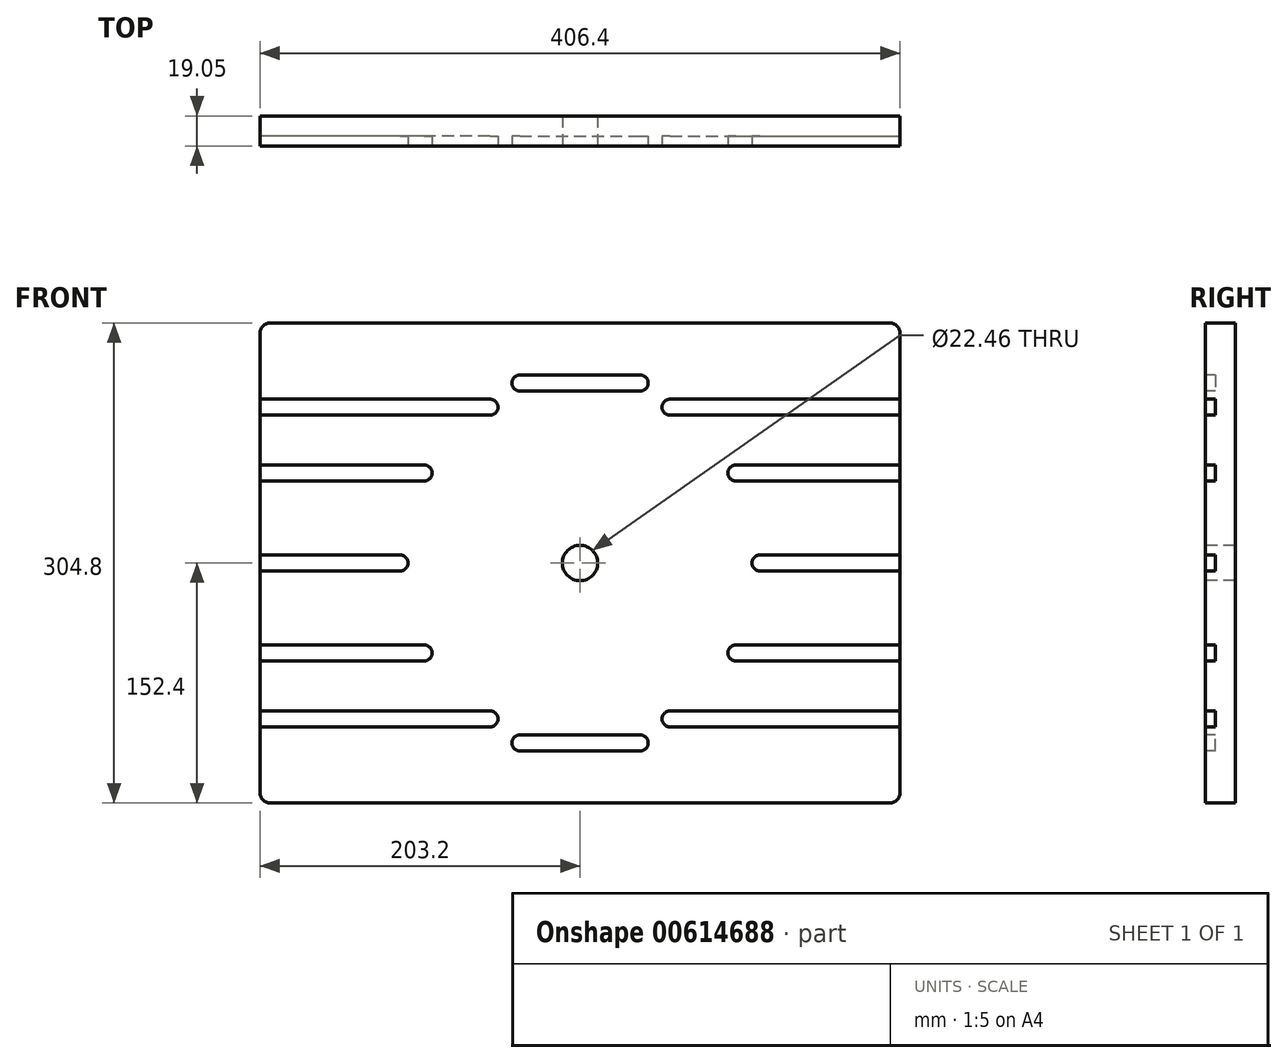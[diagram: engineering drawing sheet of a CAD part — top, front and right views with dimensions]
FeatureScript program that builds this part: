
annotation { "Feature Type Name" : "Feature", "Feature Type Description" : "" }
export const myFeature = defineFeature(function(context is Context, id is Id, definition is map)
    precondition{}
    {
        {
            var Q0;
            Q0=qCreatedBy(makeId("Front.planeOp"),FACE);
            var sketch = newSketch(context, id + "F0", { "sketchPlane" : qUnion([Q0])});
            skLineSegment(sketch, "E0.bottom", {"start": v(203.2, 152.4) * mm, "end": v(-203.2, 152.4) * mm});
            skLineSegment(sketch, "E0.top", {"start": v(203.2, -152.4) * mm, "end": v(-203.2, -152.4) * mm});
            skLineSegment(sketch, "E0.left", {"start": v(203.2, 152.4) * mm, "end": v(203.2, -152.4) * mm});
            skLineSegment(sketch, "E0.right", {"start": v(-203.2, 152.4) * mm, "end": v(-203.2, -152.4) * mm});
            skPoint(sketch, "E0.middle", {"position": v(0, 0) * mm});
            skCircle(sketch, "E1", {"center": v(0, 0) * mm, "radius": 114.3 * mm, "construction": true});
            skLineSegment(sketch, "E2", {"start": v(0, 0) * mm, "end": v(0, 114.3) * mm});
            skLineSegment(sketch, "E3", {"start": v(0, 0) * mm, "end": v(57.15, 98.99) * mm, "construction": true});
            skLineSegment(sketch, "E4", {"start": v(0, 0) * mm, "end": v(98.99, 57.15) * mm, "construction": true});
            skLineSegment(sketch, "E5", {"start": v(0, 0) * mm, "end": v(114.3, 0) * mm, "construction": true});
            skCircle(sketch, "E6", {"center": v(57.15, 98.99) * mm, "radius": 5.08 * mm});
            skLineSegment(sketch, "E7", {"start": v(57.15, 104.07) * mm, "end": v(203.2, 104.07) * mm});
            skLineSegment(sketch, "E8", {"start": v(57.15, 93.9) * mm, "end": v(203.2, 93.9) * mm});
            skCircle(sketch, "E9", {"center": v(98.99, 57.15) * mm, "radius": 5.08 * mm});
            skLineSegment(sketch, "E10", {"start": v(98.99, 62.23) * mm, "end": v(203.2, 62.23) * mm});
            skLineSegment(sketch, "E11", {"start": v(98.99, 52.07) * mm, "end": v(203.2, 52.07) * mm});
            skCircle(sketch, "E12", {"center": v(114.3, 0) * mm, "radius": 5.08 * mm});
            skLineSegment(sketch, "E13", {"start": v(114.3, 5.08) * mm, "end": v(203.2, 5.08) * mm});
            skLineSegment(sketch, "E14", {"start": v(114.3, -5.08) * mm, "end": v(203.2, -5.08) * mm});
            skLineSegment(sketch, "E15", {"start": v(-203.2, 119.38) * mm, "end": v(203.2, 119.38) * mm});
            skLineSegment(sketch, "E16", {"start": v(-203.2, 109.22) * mm, "end": v(203.2, 109.22) * mm});
            skLineSegment(sketch, "E17", {"start": v(0, 0) * mm, "end": v(98.99, -57.15) * mm, "construction": true});
            skLineSegment(sketch, "E18", {"start": v(0, 0) * mm, "end": v(57.15, -98.99) * mm, "construction": true});
            skLineSegment(sketch, "E19", {"start": v(0, 0) * mm, "end": v(0, -114.3) * mm});
            skCircle(sketch, "E20", {"center": v(98.99, -57.15) * mm, "radius": 5.08 * mm});
            skLineSegment(sketch, "E21", {"start": v(98.99, -52.07) * mm, "end": v(203.2, -52.07) * mm});
            skLineSegment(sketch, "E22", {"start": v(98.99, -62.23) * mm, "end": v(203.2, -62.23) * mm});
            skCircle(sketch, "E23", {"center": v(57.15, -98.99) * mm, "radius": 5.08 * mm});
            skLineSegment(sketch, "E24", {"start": v(57.15, -93.9) * mm, "end": v(203.2, -93.9) * mm});
            skLineSegment(sketch, "E25", {"start": v(57.15, -104.07) * mm, "end": v(203.2, -104.07) * mm});
            skArc(sketch, "E26", {"start": v(-38.24, 119.38) * mm, "mid": v(-43.32, 114.3) * mm, "end": v(-38.24, 109.22) * mm});
            skArc(sketch, "E27", {"start": v(-42.56, 116.96) * mm, "mid": v(-42.53, 118.57) * mm, "end": v(-43.92, 119.38) * mm});
            skArc(sketch, "E28", {"start": v(-43.92, 109.22) * mm, "mid": v(-42.53, 110.03) * mm, "end": v(-42.56, 111.64) * mm});
            skArc(sketch, "E29", {"start": v(-12.84, 119.38) * mm, "mid": v(-17.92, 114.3) * mm, "end": v(-12.84, 109.22) * mm});
            skArc(sketch, "E30", {"start": v(12.84, 109.22) * mm, "mid": v(17.92, 114.3) * mm, "end": v(12.84, 119.38) * mm});
            skArc(sketch, "E31", {"start": v(38.24, 109.22) * mm, "mid": v(43.32, 114.3) * mm, "end": v(38.24, 119.38) * mm});
            skLineSegment(sketch, "E32", {"start": v(-12.84, 114.3) * mm, "end": v(12.84, 114.3) * mm});
            skArc(sketch, "E33", {"start": v(43.92, 119.38) * mm, "mid": v(42.53, 118.57) * mm, "end": v(42.56, 116.96) * mm});
            skArc(sketch, "E34", {"start": v(42.56, 111.64) * mm, "mid": v(42.53, 110.03) * mm, "end": v(43.92, 109.22) * mm});
            skCircle(sketch, "E35", {"center": v(0, 0) * mm, "radius": 11.23 * mm});
            skSolve(sketch);
        }
        {
            var Q0;
            Q0 = qSketchRegion(id + "F0", true);
            var Q1;
            {var subQ0=sQuery(id+"F0.wireOp",EDGE,"E6");var subQ1=makeQuery(id+"F0.imprint","INTERSECT",VERTEX,{"derivedFrom":[subQ0,sQuery(id+"F0.wireOp",EDGE,"E7")]});Q1=makeQuery(id+"F0.imprint","IMPRINT",FACE,{"disambiguationData":[TD([[makeQuery(id+"F0.imprint","IMPRINT",EDGE,{"disambiguationData":[TD([[subQ1,-1.0]])],"derivedFrom":subQ0}),1.0]])]});}
            var Q2;
            {var subQ0=sQuery(id+"F0.wireOp",EDGE,"E9");var subQ1=makeQuery(id+"F0.imprint","INTERSECT",VERTEX,{"derivedFrom":[subQ0,sQuery(id+"F0.wireOp",EDGE,"E10")]});Q2=makeQuery(id+"F0.imprint","IMPRINT",FACE,{"disambiguationData":[TD([[makeQuery(id+"F0.imprint","IMPRINT",EDGE,{"disambiguationData":[TD([[subQ1,-1.0]])],"derivedFrom":subQ0}),1.0]])]});}
            var Q3;
            {var subQ0=sQuery(id+"F0.wireOp",EDGE,"E12");var subQ1=makeQuery(id+"F0.imprint","INTERSECT",VERTEX,{"derivedFrom":[subQ0,sQuery(id+"F0.wireOp",EDGE,"E13")]});Q3=makeQuery(id+"F0.imprint","IMPRINT",FACE,{"disambiguationData":[TD([[makeQuery(id+"F0.imprint","IMPRINT",EDGE,{"disambiguationData":[TD([[subQ1,-1.0]])],"derivedFrom":subQ0}),1.0]])]});}
            var Q4;
            {var subQ0=sQuery(id+"F0.wireOp",EDGE,"E20");var subQ1=makeQuery(id+"F0.imprint","INTERSECT",VERTEX,{"derivedFrom":[subQ0,sQuery(id+"F0.wireOp",EDGE,"E21")]});Q4=makeQuery(id+"F0.imprint","IMPRINT",FACE,{"disambiguationData":[TD([[makeQuery(id+"F0.imprint","IMPRINT",EDGE,{"disambiguationData":[TD([[subQ1,-1.0]])],"derivedFrom":subQ0}),1.0]])]});}
            var Q5;
            {var subQ0=sQuery(id+"F0.wireOp",EDGE,"E23");var subQ1=makeQuery(id+"F0.imprint","INTERSECT",VERTEX,{"derivedFrom":[subQ0,sQuery(id+"F0.wireOp",EDGE,"E24")]});Q5=makeQuery(id+"F0.imprint","IMPRINT",FACE,{"disambiguationData":[TD([[makeQuery(id+"F0.imprint","IMPRINT",EDGE,{"disambiguationData":[TD([[subQ1,-1.0]])],"derivedFrom":subQ0}),1.0]])]});}
            var Q6;
            {var subQ3=sQuery(id+"F0.wireOp",EDGE,"E33");Q6=makeQuery(id+"F0.imprint","IMPRINT",FACE,{"disambiguationData":[TD([[makeQuery(id+"F0.imprint","IMPRINT",EDGE,{"derivedFrom":subQ3}),-1.0]])]});}
            var Q7;
            {var subQ4=sQuery(id+"F0.wireOp",EDGE,"E30");Q7=makeQuery(id+"F0.imprint","IMPRINT",FACE,{"disambiguationData":[TD([[makeQuery(id+"F0.imprint","IMPRINT",EDGE,{"derivedFrom":subQ4}),-1.0]])]});}
            var Q8;
            {var subQ3=sQuery(id+"F0.wireOp",EDGE,"E34");Q8=makeQuery(id+"F0.imprint","IMPRINT",FACE,{"disambiguationData":[TD([[makeQuery(id+"F0.imprint","IMPRINT",EDGE,{"derivedFrom":subQ3}),-1.0]])]});}
            var Q9;
            {var subQ3=sQuery(id+"F0.wireOp",EDGE,"E29");Q9=makeQuery(id+"F0.imprint","IMPRINT",FACE,{"disambiguationData":[TD([[makeQuery(id+"F0.imprint","IMPRINT",EDGE,{"derivedFrom":subQ3}),1.0]])]});}
            var Q10;
            {var subQ3=sQuery(id+"F0.wireOp",EDGE,"E27");Q10=makeQuery(id+"F0.imprint","IMPRINT",FACE,{"disambiguationData":[TD([[makeQuery(id+"F0.imprint","IMPRINT",EDGE,{"derivedFrom":subQ3}),-1.0]])]});}
            var Q11;
            {var subQ5=sQuery(id+"F0.wireOp",EDGE,"E29");Q11=makeQuery(id+"F0.imprint","IMPRINT",FACE,{"disambiguationData":[TD([[makeQuery(id+"F0.imprint","IMPRINT",EDGE,{"derivedFrom":subQ5}),-1.0]])]});}
            var Q12;
            {var subQ3=sQuery(id+"F0.wireOp",EDGE,"E28");Q12=makeQuery(id+"F0.imprint","IMPRINT",FACE,{"disambiguationData":[TD([[makeQuery(id+"F0.imprint","IMPRINT",EDGE,{"derivedFrom":subQ3}),-1.0]])]});}
            extrude(context, id + "F1", {"entities" : qUnion([Q0, Q1, Q2, Q3, Q4, Q5, Q6, Q7, Q8, Q9, Q10, Q11, Q12]), "oppositeDirection" : true, "depth" : 19.05 * mm, "offsetDistance" : 25.4 * mm});
        }
        {
            var Q0;
            {var subQ0=sQuery(id+"F0.wireOp",EDGE,"E7");Q0=makeQuery(id+"F0.imprint","IMPRINT",FACE,{"disambiguationData":[TD([[makeQuery(id+"F0.imprint","IMPRINT",EDGE,{"derivedFrom":subQ0}),-1.0]])]});}
            var Q1;
            {var subQ0=sQuery(id+"F0.wireOp",EDGE,"E10");Q1=makeQuery(id+"F0.imprint","IMPRINT",FACE,{"disambiguationData":[TD([[makeQuery(id+"F0.imprint","IMPRINT",EDGE,{"derivedFrom":subQ0}),-1.0]])]});}
            var Q2;
            {var subQ0=sQuery(id+"F0.wireOp",EDGE,"E6");var subQ1=makeQuery(id+"F0.imprint","INTERSECT",VERTEX,{"derivedFrom":[subQ0,sQuery(id+"F0.wireOp",EDGE,"E7")]});Q2=makeQuery(id+"F0.imprint","IMPRINT",FACE,{"disambiguationData":[TD([[makeQuery(id+"F0.imprint","IMPRINT",EDGE,{"disambiguationData":[TD([[subQ1,-1.0]])],"derivedFrom":subQ0}),1.0]])]});}
            var Q3;
            {var subQ0=sQuery(id+"F0.wireOp",EDGE,"E9");var subQ1=makeQuery(id+"F0.imprint","INTERSECT",VERTEX,{"derivedFrom":[subQ0,sQuery(id+"F0.wireOp",EDGE,"E10")]});Q3=makeQuery(id+"F0.imprint","IMPRINT",FACE,{"disambiguationData":[TD([[makeQuery(id+"F0.imprint","IMPRINT",EDGE,{"disambiguationData":[TD([[subQ1,-1.0]])],"derivedFrom":subQ0}),1.0]])]});}
            var Q4;
            {var subQ0=sQuery(id+"F0.wireOp",EDGE,"E12");var subQ1=makeQuery(id+"F0.imprint","INTERSECT",VERTEX,{"derivedFrom":[subQ0,sQuery(id+"F0.wireOp",EDGE,"E13")]});Q4=makeQuery(id+"F0.imprint","IMPRINT",FACE,{"disambiguationData":[TD([[makeQuery(id+"F0.imprint","IMPRINT",EDGE,{"disambiguationData":[TD([[subQ1,-1.0]])],"derivedFrom":subQ0}),1.0]])]});}
            var Q5;
            {var subQ0=sQuery(id+"F0.wireOp",EDGE,"E13");Q5=makeQuery(id+"F0.imprint","IMPRINT",FACE,{"disambiguationData":[TD([[makeQuery(id+"F0.imprint","IMPRINT",EDGE,{"derivedFrom":subQ0}),-1.0]])]});}
            var Q6;
            {var subQ0=sQuery(id+"F0.wireOp",EDGE,"E20");var subQ1=makeQuery(id+"F0.imprint","INTERSECT",VERTEX,{"derivedFrom":[subQ0,sQuery(id+"F0.wireOp",EDGE,"E21")]});Q6=makeQuery(id+"F0.imprint","IMPRINT",FACE,{"disambiguationData":[TD([[makeQuery(id+"F0.imprint","IMPRINT",EDGE,{"disambiguationData":[TD([[subQ1,-1.0]])],"derivedFrom":subQ0}),1.0]])]});}
            var Q7;
            {var subQ0=sQuery(id+"F0.wireOp",EDGE,"E21");Q7=makeQuery(id+"F0.imprint","IMPRINT",FACE,{"disambiguationData":[TD([[makeQuery(id+"F0.imprint","IMPRINT",EDGE,{"derivedFrom":subQ0}),-1.0]])]});}
            var Q8;
            {var subQ0=sQuery(id+"F0.wireOp",EDGE,"E23");var subQ1=makeQuery(id+"F0.imprint","INTERSECT",VERTEX,{"derivedFrom":[subQ0,sQuery(id+"F0.wireOp",EDGE,"E24")]});Q8=makeQuery(id+"F0.imprint","IMPRINT",FACE,{"disambiguationData":[TD([[makeQuery(id+"F0.imprint","IMPRINT",EDGE,{"disambiguationData":[TD([[subQ1,-1.0]])],"derivedFrom":subQ0}),1.0]])]});}
            var Q9;
            {var subQ0=sQuery(id+"F0.wireOp",EDGE,"E24");Q9=makeQuery(id+"F0.imprint","IMPRINT",FACE,{"disambiguationData":[TD([[makeQuery(id+"F0.imprint","IMPRINT",EDGE,{"derivedFrom":subQ0}),-1.0]])]});}
            var Q10;
            {var subQ4=sQuery(id+"F0.wireOp",EDGE,"E30");Q10=makeQuery(id+"F0.imprint","IMPRINT",FACE,{"disambiguationData":[TD([[makeQuery(id+"F0.imprint","IMPRINT",EDGE,{"derivedFrom":subQ4}),-1.0]])]});}
            var Q11;
            {var subQ3=sQuery(id+"F0.wireOp",EDGE,"E29");Q11=makeQuery(id+"F0.imprint","IMPRINT",FACE,{"disambiguationData":[TD([[makeQuery(id+"F0.imprint","IMPRINT",EDGE,{"derivedFrom":subQ3}),1.0]])]});}
            var Q12;
            {var subQ5=sQuery(id+"F0.wireOp",EDGE,"E29");Q12=makeQuery(id+"F0.imprint","IMPRINT",FACE,{"disambiguationData":[TD([[makeQuery(id+"F0.imprint","IMPRINT",EDGE,{"derivedFrom":subQ5}),-1.0]])]});}
            extrude(context, id + "F2", {"entities" : qUnion([Q0, Q1, Q2, Q3, Q4, Q5, Q6, Q7, Q8, Q9, Q10, Q11, Q12]), "operationType" : NewBodyOperationType.REMOVE, "oppositeDirection" : true, "depth" : 6.35 * mm, "offsetDistance" : 25.4 * mm});
        }
        {
            var Q0;
            {var subQ0=sQuery(id+"F0.wireOp",EDGE,"E7");Q0=makeQuery(id+"F0.imprint","IMPRINT",FACE,{"disambiguationData":[TD([[makeQuery(id+"F0.imprint","IMPRINT",EDGE,{"derivedFrom":subQ0}),-1.0]])]});}
            var Q1;
            {var subQ0=sQuery(id+"F0.wireOp",EDGE,"E6");var subQ1=makeQuery(id+"F0.imprint","INTERSECT",VERTEX,{"derivedFrom":[subQ0,sQuery(id+"F0.wireOp",EDGE,"E7")]});Q1=makeQuery(id+"F0.imprint","IMPRINT",FACE,{"disambiguationData":[TD([[makeQuery(id+"F0.imprint","IMPRINT",EDGE,{"disambiguationData":[TD([[subQ1,-1.0]])],"derivedFrom":subQ0}),1.0]])]});}
            var Q2;
            {var subQ0=sQuery(id+"F0.wireOp",EDGE,"E10");Q2=makeQuery(id+"F0.imprint","IMPRINT",FACE,{"disambiguationData":[TD([[makeQuery(id+"F0.imprint","IMPRINT",EDGE,{"derivedFrom":subQ0}),-1.0]])]});}
            var Q3;
            {var subQ0=sQuery(id+"F0.wireOp",EDGE,"E9");var subQ1=makeQuery(id+"F0.imprint","INTERSECT",VERTEX,{"derivedFrom":[subQ0,sQuery(id+"F0.wireOp",EDGE,"E10")]});Q3=makeQuery(id+"F0.imprint","IMPRINT",FACE,{"disambiguationData":[TD([[makeQuery(id+"F0.imprint","IMPRINT",EDGE,{"disambiguationData":[TD([[subQ1,-1.0]])],"derivedFrom":subQ0}),1.0]])]});}
            var Q4;
            {var subQ0=sQuery(id+"F0.wireOp",EDGE,"E12");var subQ1=makeQuery(id+"F0.imprint","INTERSECT",VERTEX,{"derivedFrom":[subQ0,sQuery(id+"F0.wireOp",EDGE,"E13")]});Q4=makeQuery(id+"F0.imprint","IMPRINT",FACE,{"disambiguationData":[TD([[makeQuery(id+"F0.imprint","IMPRINT",EDGE,{"disambiguationData":[TD([[subQ1,-1.0]])],"derivedFrom":subQ0}),1.0]])]});}
            var Q5;
            {var subQ0=sQuery(id+"F0.wireOp",EDGE,"E13");Q5=makeQuery(id+"F0.imprint","IMPRINT",FACE,{"disambiguationData":[TD([[makeQuery(id+"F0.imprint","IMPRINT",EDGE,{"derivedFrom":subQ0}),-1.0]])]});}
            var Q6;
            {var subQ0=sQuery(id+"F0.wireOp",EDGE,"E20");var subQ1=makeQuery(id+"F0.imprint","INTERSECT",VERTEX,{"derivedFrom":[subQ0,sQuery(id+"F0.wireOp",EDGE,"E21")]});Q6=makeQuery(id+"F0.imprint","IMPRINT",FACE,{"disambiguationData":[TD([[makeQuery(id+"F0.imprint","IMPRINT",EDGE,{"disambiguationData":[TD([[subQ1,-1.0]])],"derivedFrom":subQ0}),1.0]])]});}
            var Q7;
            {var subQ0=sQuery(id+"F0.wireOp",EDGE,"E21");Q7=makeQuery(id+"F0.imprint","IMPRINT",FACE,{"disambiguationData":[TD([[makeQuery(id+"F0.imprint","IMPRINT",EDGE,{"derivedFrom":subQ0}),-1.0]])]});}
            var Q8;
            {var subQ0=sQuery(id+"F0.wireOp",EDGE,"E23");var subQ1=makeQuery(id+"F0.imprint","INTERSECT",VERTEX,{"derivedFrom":[subQ0,sQuery(id+"F0.wireOp",EDGE,"E24")]});Q8=makeQuery(id+"F0.imprint","IMPRINT",FACE,{"disambiguationData":[TD([[makeQuery(id+"F0.imprint","IMPRINT",EDGE,{"disambiguationData":[TD([[subQ1,-1.0]])],"derivedFrom":subQ0}),1.0]])]});}
            var Q9;
            {var subQ0=sQuery(id+"F0.wireOp",EDGE,"E24");Q9=makeQuery(id+"F0.imprint","IMPRINT",FACE,{"disambiguationData":[TD([[makeQuery(id+"F0.imprint","IMPRINT",EDGE,{"derivedFrom":subQ0}),-1.0]])]});}
            var Q10;
            {var subQ5=sQuery(id+"F0.wireOp",EDGE,"E29");Q10=makeQuery(id+"F0.imprint","IMPRINT",FACE,{"disambiguationData":[TD([[makeQuery(id+"F0.imprint","IMPRINT",EDGE,{"derivedFrom":subQ5}),-1.0]])]});}
            var Q11;
            {var subQ3=sQuery(id+"F0.wireOp",EDGE,"E29");Q11=makeQuery(id+"F0.imprint","IMPRINT",FACE,{"disambiguationData":[TD([[makeQuery(id+"F0.imprint","IMPRINT",EDGE,{"derivedFrom":subQ3}),1.0]])]});}
            var Q12;
            {var subQ4=sQuery(id+"F0.wireOp",EDGE,"E30");Q12=makeQuery(id+"F0.imprint","IMPRINT",FACE,{"disambiguationData":[TD([[makeQuery(id+"F0.imprint","IMPRINT",EDGE,{"derivedFrom":subQ4}),-1.0]])]});}
            extrude(context, id + "F3", {"entities" : qUnion([Q0, Q1, Q2, Q3, Q4, Q5, Q6, Q7, Q8, Q9, Q10, Q11, Q12]), "oppositeDirection" : true, "depth" : 6.35 * mm, "offsetDistance" : 25.4 * mm});
        }
        {
            var Q0;
            Q0=makeQuery(id+"F3.opExtrude","SWEPT_BODY",BODY,{"disambiguationData":[OSD([sQuery(id+"F0.wireOp",EDGE,"E0.left"),sQuery(id+"F0.wireOp",EDGE,"E0.right"),sQuery(id+"F0.wireOp",EDGE,"E15"),sQuery(id+"F0.wireOp",EDGE,"E16")])]});
            var Q1;
            Q1=makeQuery(id+"F3.opExtrude","SWEPT_BODY",BODY,{"disambiguationData":[OSD([sQuery(id+"F0.wireOp",EDGE,"E0.left"),sQuery(id+"F0.wireOp",EDGE,"E6"),sQuery(id+"F0.wireOp",EDGE,"E7"),sQuery(id+"F0.wireOp",EDGE,"E8")])]});
            var Q2;
            Q2=makeQuery(id+"F3.opExtrude","SWEPT_BODY",BODY,{"disambiguationData":[OSD([sQuery(id+"F0.wireOp",EDGE,"E0.left"),sQuery(id+"F0.wireOp",EDGE,"E9"),sQuery(id+"F0.wireOp",EDGE,"E10"),sQuery(id+"F0.wireOp",EDGE,"E11")])]});
            var Q3;
            Q3=makeQuery(id+"F3.opExtrude","SWEPT_BODY",BODY,{"disambiguationData":[OSD([sQuery(id+"F0.wireOp",EDGE,"E0.left"),sQuery(id+"F0.wireOp",EDGE,"E12"),sQuery(id+"F0.wireOp",EDGE,"E13"),sQuery(id+"F0.wireOp",EDGE,"E14")])]});
            var Q4;
            Q4=makeQuery(id+"F3.opExtrude","SWEPT_BODY",BODY,{"disambiguationData":[OSD([sQuery(id+"F0.wireOp",EDGE,"E0.left"),sQuery(id+"F0.wireOp",EDGE,"E20"),sQuery(id+"F0.wireOp",EDGE,"E21"),sQuery(id+"F0.wireOp",EDGE,"E22")])]});
            var Q5;
            Q5=makeQuery(id+"F3.opExtrude","SWEPT_BODY",BODY,{"disambiguationData":[OSD([sQuery(id+"F0.wireOp",EDGE,"E0.left"),sQuery(id+"F0.wireOp",EDGE,"E23"),sQuery(id+"F0.wireOp",EDGE,"E24"),sQuery(id+"F0.wireOp",EDGE,"E25")])]});
            var Q6;
            Q6=sQuery(id+"F0.wireOp",EDGE,"E1");
            circularPattern(context, id + "F4", {"entities" : qUnion([Q0, Q1, Q2, Q3, Q4, Q5]), "axis" : qUnion([Q6]), "angle" : 360 * degree, "instanceCount" : 2, "equalSpace" : true});
        }
        {
            var Q0;
            Q0=makeQuery(id+"F1.opExtrude","SWEPT_EDGE",EDGE,{"disambiguationData":[OSD([sQuery(id+"F0.wireOp",EDGE,"E0.bottom"),sQuery(id+"F0.wireOp",EDGE,"E0.left")])]});
            var Q1;
            Q1=makeQuery(id+"F1.opExtrude","SWEPT_EDGE",EDGE,{"disambiguationData":[OSD([sQuery(id+"F0.wireOp",EDGE,"E0.bottom"),sQuery(id+"F0.wireOp",EDGE,"E0.right")])]});
            var Q2;
            Q2=makeQuery(id+"F1.opExtrude","SWEPT_EDGE",EDGE,{"disambiguationData":[OSD([sQuery(id+"F0.wireOp",EDGE,"E0.top"),sQuery(id+"F0.wireOp",EDGE,"E0.left")])]});
            var Q3;
            Q3=makeQuery(id+"F1.opExtrude","SWEPT_EDGE",EDGE,{"disambiguationData":[OSD([sQuery(id+"F0.wireOp",EDGE,"E0.top"),sQuery(id+"F0.wireOp",EDGE,"E0.right")])]});
            fillet(context, id + "F5", {"entities" : qUnion([Q0, Q1, Q2, Q3]), "radius" : 6.35 * mm, "tangentPropagation" : true, "allowEdgeOverflow" : false});
        }
    });
